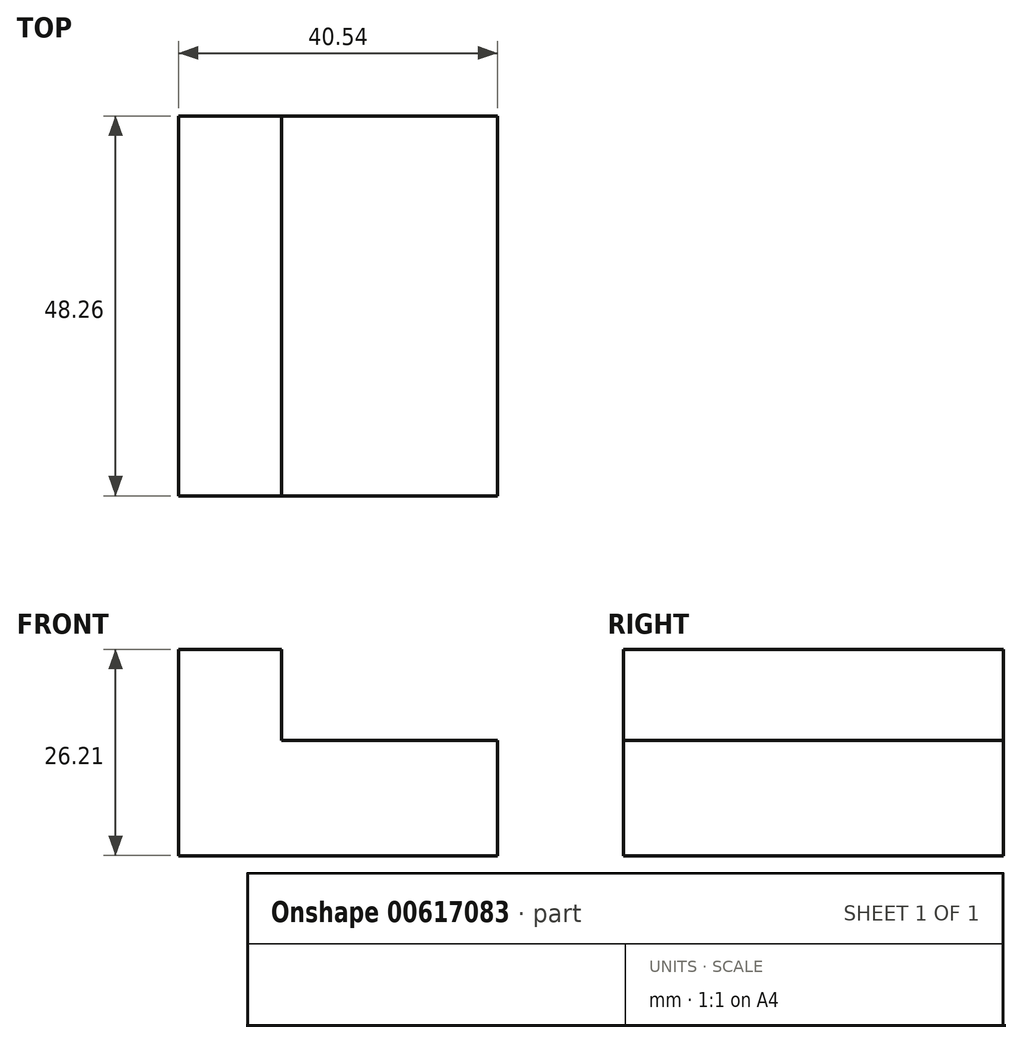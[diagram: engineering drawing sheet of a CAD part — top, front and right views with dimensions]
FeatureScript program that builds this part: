
annotation { "Feature Type Name" : "Feature", "Feature Type Description" : "" }
export const myFeature = defineFeature(function(context is Context, id is Id, definition is map)
    precondition{}
    {
        {
            var Q0;
            Q0=qCreatedBy(makeId("Front.planeOp"),FACE);
            var sketch = newSketch(context, id + "F0", { "sketchPlane" : qUnion([Q0])});
            skLineSegment(sketch, "E0", {"start": v(-30.94, 0) * mm, "end": v(-30.94, -26.21) * mm});
            skLineSegment(sketch, "E1", {"start": v(-30.94, -26.21) * mm, "end": v(9.6, -26.21) * mm});
            skLineSegment(sketch, "E2", {"start": v(9.6, -26.21) * mm, "end": v(9.6, -11.58) * mm});
            skLineSegment(sketch, "E3", {"start": v(9.6, -11.58) * mm, "end": v(-17.83, -11.58) * mm});
            skLineSegment(sketch, "E4", {"start": v(-17.83, -11.58) * mm, "end": v(-17.83, 0) * mm});
            skLineSegment(sketch, "E5", {"start": v(-17.83, 0) * mm, "end": v(-30.94, 0) * mm});
            skSolve(sketch);
        }
        {
            var Q0;
            Q0 = qSketchRegion(id + "F0", true);
            extrude(context, id + "F1", {"entities" : qUnion([Q0]), "depth" : 48.26 * mm, "offsetDistance" : 25.4 * mm});
        }
    });
